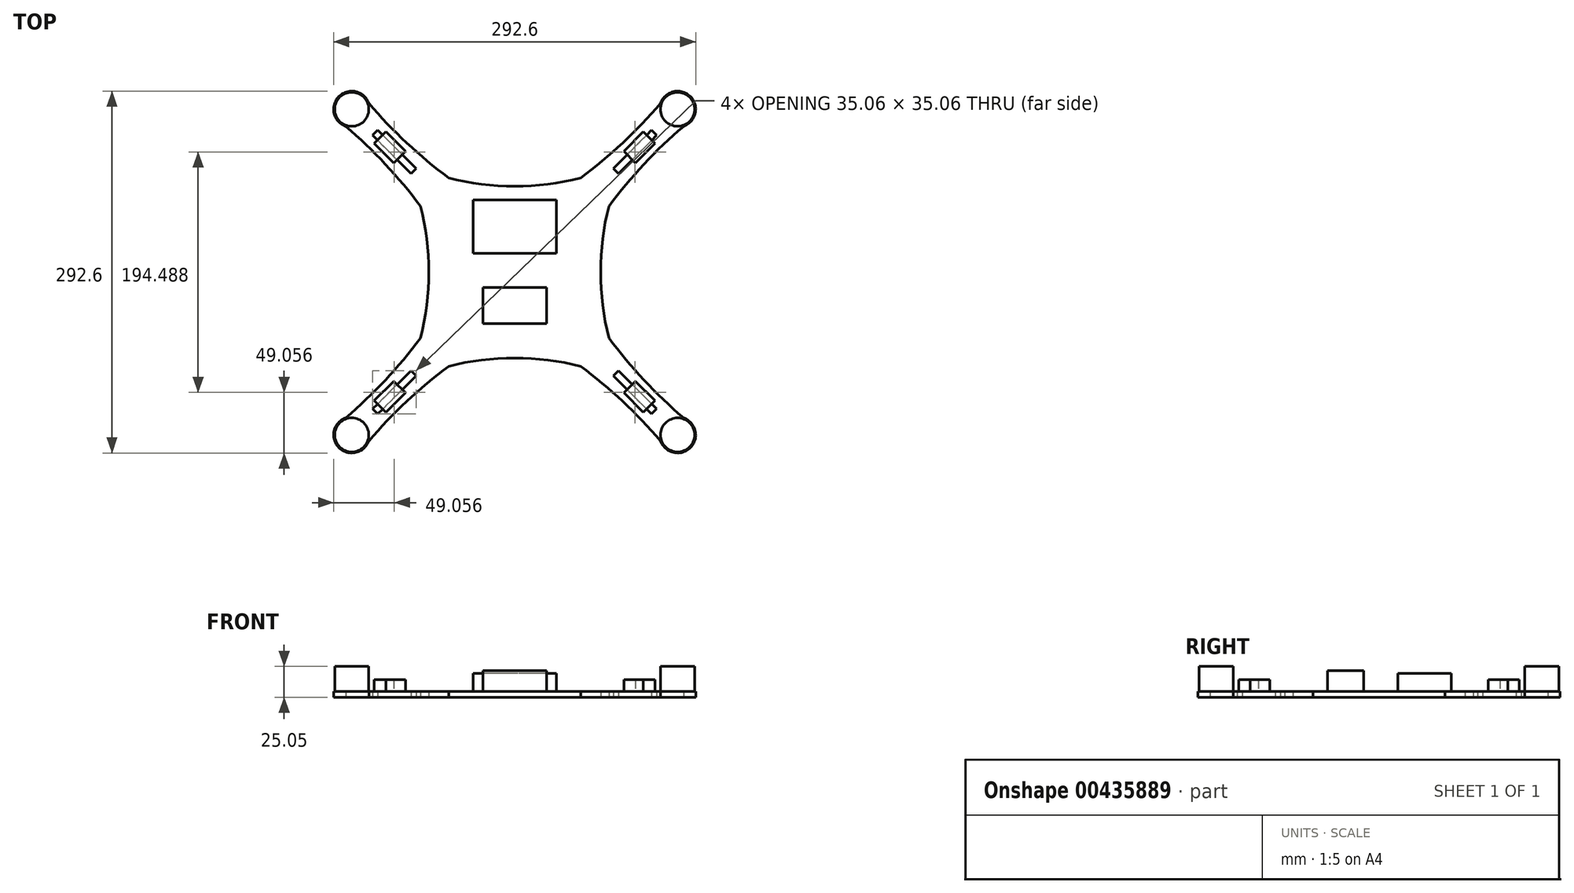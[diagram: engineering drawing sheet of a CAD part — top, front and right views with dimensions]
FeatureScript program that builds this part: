
annotation { "Feature Type Name" : "Feature", "Feature Type Description" : "" }
export const myFeature = defineFeature(function(context is Context, id is Id, definition is map)
    precondition{}
    {
        {
            var Q0;
            Q0=qCreatedBy(makeId("Top.planeOp"),FACE);
            var sketch = newSketch(context, id + "F0", { "sketchPlane" : qUnion([Q0])});
            skArc(sketch, "E0", {"start": v(-122.78, 142.2) * mm, "mid": v(-147.94, 147.94) * mm, "end": v(-142.2, 122.78) * mm});
            skArc(sketch, "E1.MirrorC", {"start": v(122.78, 142.2) * mm, "mid": v(147.94, 147.94) * mm, "end": v(142.2, 122.78) * mm});
            skArc(sketch, "E2.MirrorC", {"start": v(-122.78, -142.2) * mm, "mid": v(-147.94, -147.94) * mm, "end": v(-142.2, -122.78) * mm});
            skArc(sketch, "E3.MirrorC", {"start": v(122.78, -142.2) * mm, "mid": v(147.94, -147.94) * mm, "end": v(142.2, -122.78) * mm});
            skArc(sketch, "E4", {"start": v(79.33, 55.58) * mm, "mid": v(72.4, 0) * mm, "end": v(79.33, -55.58) * mm});
            skArc(sketch, "E5.MirrorCS", {"start": v(-79.33, 55.58) * mm, "mid": v(-72.4, 0) * mm, "end": v(-79.33, -55.58) * mm});
            skArc(sketch, "E6.1.0", {"start": v(-55.58, 79.33) * mm, "mid": v(0, 72.4) * mm, "end": v(55.58, 79.33) * mm});
            skArc(sketch, "E6.2.0", {"start": v(-79.33, -55.58) * mm, "mid": v(-72.4, 0) * mm, "end": v(-79.33, 55.58) * mm});
            skArc(sketch, "E6.3.0", {"start": v(55.58, -79.33) * mm, "mid": v(0, -72.4) * mm, "end": v(-55.58, -79.33) * mm});
            skArc(sketch, "E7", {"start": v(-142.2, -122.78) * mm, "mid": v(-108.9, -90.93) * mm, "end": v(-79.33, -55.58) * mm});
            skArc(sketch, "E8.MirrorCS", {"start": v(-122.78, -142.2) * mm, "mid": v(-90.93, -108.9) * mm, "end": v(-55.58, -79.33) * mm});
            skArc(sketch, "E9.MirrorCS", {"start": v(-142.2, 122.78) * mm, "mid": v(-108.9, 90.93) * mm, "end": v(-79.33, 55.58) * mm});
            skArc(sketch, "E10.MirrorCS", {"start": v(-122.78, 142.2) * mm, "mid": v(-90.93, 108.9) * mm, "end": v(-55.58, 79.33) * mm});
            skArc(sketch, "E11.MirrorCS", {"start": v(142.2, -122.78) * mm, "mid": v(108.9, -90.93) * mm, "end": v(79.33, -55.58) * mm});
            skArc(sketch, "E12.MirrorCS", {"start": v(122.78, -142.2) * mm, "mid": v(90.93, -108.9) * mm, "end": v(55.58, -79.33) * mm});
            skArc(sketch, "E13.MirrorCS", {"start": v(142.2, 122.78) * mm, "mid": v(108.9, 90.93) * mm, "end": v(79.33, 55.58) * mm});
            skArc(sketch, "E14.MirrorCS", {"start": v(122.78, 142.2) * mm, "mid": v(90.93, 108.9) * mm, "end": v(55.58, 79.33) * mm});
            skLineSegment(sketch, "E15", {"start": v(-117.4, 117.4) * mm, "end": v(-119.56, 115.25) * mm});
            skLineSegment(sketch, "E16", {"start": v(-87.34, 83.04) * mm, "end": v(-85.19, 85.19) * mm});
            skLineSegment(sketch, "E17.MirrorCS", {"start": v(-117.4, 117.4) * mm, "end": v(-115.25, 119.56) * mm});
            skLineSegment(sketch, "E18.MirrorCS", {"start": v(-83.04, 87.34) * mm, "end": v(-85.19, 85.19) * mm});
            skLineSegment(sketch, "E19", {"start": v(-119.56, 115.25) * mm, "end": v(-87.34, 83.04) * mm});
            skLineSegment(sketch, "E20", {"start": v(-115.25, 119.56) * mm, "end": v(-83.04, 87.34) * mm});
            skPoint(sketch, "E21.orphan", {"position": v(-113.1, 121.71) * mm});
            skPoint(sketch, "E22.orphan", {"position": v(-80.88, 89.5) * mm});
            skPoint(sketch, "E23.end.orphan", {"position": v(-89.5, 80.88) * mm});
            skPoint(sketch, "E24.orphan", {"position": v(-121.71, 113.1) * mm});
            skLineSegment(sketch, "E25", {"start": v(83.04, 87.34) * mm, "end": v(115.25, 119.56) * mm});
            skLineSegment(sketch, "E26", {"start": v(115.25, 119.56) * mm, "end": v(119.56, 115.25) * mm});
            skLineSegment(sketch, "E27", {"start": v(119.56, 115.25) * mm, "end": v(87.34, 83.04) * mm});
            skLineSegment(sketch, "E28", {"start": v(83.04, 87.34) * mm, "end": v(87.34, 83.04) * mm});
            skLineSegment(sketch, "E29", {"start": v(83.04, -87.34) * mm, "end": v(115.25, -119.56) * mm});
            skLineSegment(sketch, "E30", {"start": v(115.25, -119.56) * mm, "end": v(119.56, -115.25) * mm});
            skLineSegment(sketch, "E31", {"start": v(119.56, -115.25) * mm, "end": v(87.34, -83.04) * mm});
            skLineSegment(sketch, "E32", {"start": v(87.34, -83.04) * mm, "end": v(83.04, -87.34) * mm});
            skLineSegment(sketch, "E33", {"start": v(-119.56, -115.25) * mm, "end": v(-87.34, -83.04) * mm});
            skLineSegment(sketch, "E34", {"start": v(-87.34, -83.04) * mm, "end": v(-83.04, -87.34) * mm});
            skLineSegment(sketch, "E35", {"start": v(-83.04, -87.34) * mm, "end": v(-115.25, -119.56) * mm});
            skLineSegment(sketch, "E36", {"start": v(-115.25, -119.56) * mm, "end": v(-119.56, -115.25) * mm});
            skSolve(sketch);
        }
        {
            var Q0;
            Q0=makeQuery(id+"F0.imprint","IMPRINT",FACE,{"disambiguationData":[TD([[makeQuery(id+"F0.imprint","IMPRINT",EDGE,{"derivedFrom":sQuery(id+"F0.wireOp",EDGE,"E0")}),1.0]])]});
            extrude(context, id + "F1", {"entities" : qUnion([Q0]), "depth" : 4.76 * mm});
        }
        {
            var Q0;
            Q0=makeQuery(id+"F1.opExtrude","CAP_FACE",FACE,{"disambiguationData":[OSD([sQuery(id+"F0.wireOp",EDGE,"E0"),sQuery(id+"F0.wireOp",EDGE,"E1.MirrorC"),sQuery(id+"F0.wireOp",EDGE,"E2.MirrorC"),sQuery(id+"F0.wireOp",EDGE,"E3.MirrorC"),sQuery(id+"F0.wireOp",EDGE,"E4"),sQuery(id+"F0.wireOp",EDGE,"E6.1.0"),sQuery(id+"F0.wireOp",EDGE,"E6.2.0"),sQuery(id+"F0.wireOp",EDGE,"E6.3.0"),sQuery(id+"F0.wireOp",EDGE,"E7"),sQuery(id+"F0.wireOp",EDGE,"E8.MirrorCS"),sQuery(id+"F0.wireOp",EDGE,"E9.MirrorCS"),sQuery(id+"F0.wireOp",EDGE,"E10.MirrorCS"),sQuery(id+"F0.wireOp",EDGE,"E11.MirrorCS"),sQuery(id+"F0.wireOp",EDGE,"E12.MirrorCS"),sQuery(id+"F0.wireOp",EDGE,"E13.MirrorCS"),sQuery(id+"F0.wireOp",EDGE,"E14.MirrorCS"),sQuery(id+"F0.wireOp",EDGE,"E15"),sQuery(id+"F0.wireOp",EDGE,"E16"),sQuery(id+"F0.wireOp",EDGE,"E17.MirrorCS"),sQuery(id+"F0.wireOp",EDGE,"E18.MirrorCS"),sQuery(id+"F0.wireOp",EDGE,"E19"),sQuery(id+"F0.wireOp",EDGE,"E20"),sQuery(id+"F0.wireOp",EDGE,"E25"),sQuery(id+"F0.wireOp",EDGE,"E26"),sQuery(id+"F0.wireOp",EDGE,"E27"),sQuery(id+"F0.wireOp",EDGE,"E28"),sQuery(id+"F0.wireOp",EDGE,"E29"),sQuery(id+"F0.wireOp",EDGE,"E30"),sQuery(id+"F0.wireOp",EDGE,"E31"),sQuery(id+"F0.wireOp",EDGE,"E32"),sQuery(id+"F0.wireOp",EDGE,"E33"),sQuery(id+"F0.wireOp",EDGE,"E34"),sQuery(id+"F0.wireOp",EDGE,"E35"),sQuery(id+"F0.wireOp",EDGE,"E36")])],"isStart":false});
            var sketch = newSketch(context, id + "F2", { "sketchPlane" : qUnion([Q0])});
            skArc(sketch, "E37.0.0", {"start": v(55.58, -79.33) * mm, "mid": v(90.93, -108.9) * mm, "end": v(122.78, -142.2) * mm});
            skArc(sketch, "E37.0.1", {"start": v(122.78, -142.2) * mm, "mid": v(147.94, -147.94) * mm, "end": v(142.2, -122.78) * mm});
            skArc(sketch, "E37.0.2", {"start": v(142.2, -122.78) * mm, "mid": v(108.9, -90.93) * mm, "end": v(79.33, -55.58) * mm});
            skArc(sketch, "E37.0.3", {"start": v(79.33, -55.58) * mm, "mid": v(72.4, 0) * mm, "end": v(79.33, 55.58) * mm});
            skArc(sketch, "E37.0.4", {"start": v(79.33, 55.58) * mm, "mid": v(108.9, 90.93) * mm, "end": v(142.2, 122.78) * mm});
            skArc(sketch, "E37.0.5", {"start": v(142.2, 122.78) * mm, "mid": v(147.94, 147.94) * mm, "end": v(122.78, 142.2) * mm});
            skArc(sketch, "E37.0.6", {"start": v(122.78, 142.2) * mm, "mid": v(90.93, 108.9) * mm, "end": v(55.58, 79.33) * mm});
            skArc(sketch, "E37.0.7", {"start": v(55.58, 79.33) * mm, "mid": v(0, 72.4) * mm, "end": v(-55.58, 79.33) * mm});
            skArc(sketch, "E37.0.8", {"start": v(-55.58, 79.33) * mm, "mid": v(-90.93, 108.9) * mm, "end": v(-122.78, 142.2) * mm});
            skArc(sketch, "E37.0.9", {"start": v(-122.78, 142.2) * mm, "mid": v(-147.94, 147.94) * mm, "end": v(-142.2, 122.78) * mm});
            skArc(sketch, "E37.0.10", {"start": v(-142.2, 122.78) * mm, "mid": v(-108.9, 90.93) * mm, "end": v(-79.33, 55.58) * mm});
            skArc(sketch, "E37.0.11", {"start": v(-79.33, 55.58) * mm, "mid": v(-72.4, 0) * mm, "end": v(-79.33, -55.58) * mm});
            skArc(sketch, "E37.0.12", {"start": v(-79.33, -55.58) * mm, "mid": v(-108.9, -90.93) * mm, "end": v(-142.2, -122.78) * mm});
            skArc(sketch, "E37.0.13", {"start": v(-142.2, -122.78) * mm, "mid": v(-147.94, -147.94) * mm, "end": v(-122.78, -142.2) * mm});
            skArc(sketch, "E37.0.14", {"start": v(-122.78, -142.2) * mm, "mid": v(-90.93, -108.9) * mm, "end": v(-55.58, -79.33) * mm});
            skArc(sketch, "E37.0.15", {"start": v(-55.58, -79.33) * mm, "mid": v(0, -72.4) * mm, "end": v(55.58, -79.33) * mm});
            skCircle(sketch, "E38", {"center": v(-137.16, 137.16) * mm, "radius": 14.35 * mm});
            skCircle(sketch, "E39", {"center": v(137.16, 137.16) * mm, "radius": 14.35 * mm});
            skCircle(sketch, "E40", {"center": v(137.16, -137.16) * mm, "radius": 14.35 * mm});
            skCircle(sketch, "E41", {"center": v(-137.16, -137.16) * mm, "radius": 14.35 * mm});
            skLineSegment(sketch, "E42.bottom", {"start": v(35.05, 60.71) * mm, "end": v(-35.05, 60.71) * mm});
            skLineSegment(sketch, "E42.top", {"start": v(35.05, 15.76) * mm, "end": v(-35.05, 15.76) * mm});
            skLineSegment(sketch, "E42.left", {"start": v(35.05, 60.71) * mm, "end": v(35.05, 15.76) * mm});
            skLineSegment(sketch, "E42.right", {"start": v(-35.05, 60.71) * mm, "end": v(-35.05, 15.76) * mm});
            skPoint(sketch, "E42.middle", {"position": v(0, 38.23) * mm});
            skLineSegment(sketch, "E43.bottom", {"start": v(26.79, -13.03) * mm, "end": v(-26.79, -13.03) * mm});
            skLineSegment(sketch, "E43.top", {"start": v(26.79, -43.5) * mm, "end": v(-26.79, -43.5) * mm});
            skLineSegment(sketch, "E43.left", {"start": v(26.79, -13.03) * mm, "end": v(26.79, -43.5) * mm});
            skLineSegment(sketch, "E43.right", {"start": v(-26.79, -13.03) * mm, "end": v(-26.79, -43.5) * mm});
            skPoint(sketch, "E43.middle", {"position": v(0, -28.27) * mm});
            skLineSegment(sketch, "E44", {"start": v(-113.26, 113.26) * mm, "end": v(-118.18, 108.35) * mm});
            skLineSegment(sketch, "E45", {"start": v(-118.18, 108.35) * mm, "end": v(-101.7, 91.88) * mm});
            skLineSegment(sketch, "E46", {"start": v(-101.7, 91.88) * mm, "end": v(-96.79, 96.79) * mm});
            skLineSegment(sketch, "E47", {"start": v(0, 0) * mm, "end": v(0, 9.95) * mm});
            skLineSegment(sketch, "E48", {"start": v(0, 0) * mm, "end": v(8.33, 0) * mm});
            skLineSegment(sketch, "E49.MirrorCS", {"start": v(-113.26, 113.26) * mm, "end": v(-108.35, 118.18) * mm});
            skLineSegment(sketch, "E50.MirrorCS", {"start": v(-108.35, 118.18) * mm, "end": v(-91.88, 101.7) * mm});
            skLineSegment(sketch, "E51.MirrorCS", {"start": v(-91.88, 101.7) * mm, "end": v(-96.79, 96.79) * mm});
            skLineSegment(sketch, "E52.MirrorCS", {"start": v(113.26, 113.26) * mm, "end": v(118.18, 108.35) * mm});
            skLineSegment(sketch, "E53.MirrorCS", {"start": v(113.26, 113.26) * mm, "end": v(108.35, 118.18) * mm});
            skLineSegment(sketch, "E54.MirrorCS", {"start": v(108.35, 118.18) * mm, "end": v(91.88, 101.7) * mm});
            skLineSegment(sketch, "E55.MirrorCS", {"start": v(91.88, 101.7) * mm, "end": v(96.79, 96.79) * mm});
            skLineSegment(sketch, "E56.MirrorCS", {"start": v(101.7, 91.88) * mm, "end": v(96.79, 96.79) * mm});
            skLineSegment(sketch, "E57.MirrorCS", {"start": v(118.18, 108.35) * mm, "end": v(101.7, 91.88) * mm});
            skLineSegment(sketch, "E58.MirrorCS", {"start": v(108.35, -118.18) * mm, "end": v(91.88, -101.7) * mm});
            skLineSegment(sketch, "E59.MirrorCS", {"start": v(113.26, -113.26) * mm, "end": v(108.35, -118.18) * mm});
            skLineSegment(sketch, "E60.MirrorCS", {"start": v(113.26, -113.26) * mm, "end": v(118.18, -108.35) * mm});
            skLineSegment(sketch, "E61.MirrorCS", {"start": v(118.18, -108.35) * mm, "end": v(101.7, -91.88) * mm});
            skLineSegment(sketch, "E62.MirrorCS", {"start": v(101.7, -91.88) * mm, "end": v(96.79, -96.79) * mm});
            skLineSegment(sketch, "E63.MirrorCS", {"start": v(91.88, -101.7) * mm, "end": v(96.79, -96.79) * mm});
            skLineSegment(sketch, "E64.MirrorCS", {"start": v(-101.7, -91.88) * mm, "end": v(-96.79, -96.79) * mm});
            skLineSegment(sketch, "E65.MirrorCS", {"start": v(-91.88, -101.7) * mm, "end": v(-96.79, -96.79) * mm});
            skLineSegment(sketch, "E66.MirrorCS", {"start": v(-108.35, -118.18) * mm, "end": v(-91.88, -101.7) * mm});
            skLineSegment(sketch, "E67.MirrorCS", {"start": v(-113.26, -113.26) * mm, "end": v(-108.35, -118.18) * mm});
            skLineSegment(sketch, "E68.MirrorCS", {"start": v(-113.26, -113.26) * mm, "end": v(-118.18, -108.35) * mm});
            skLineSegment(sketch, "E69.MirrorCS", {"start": v(-118.18, -108.35) * mm, "end": v(-101.7, -91.88) * mm});
            skSolve(sketch);
        }
        {
            var Q0;
            Q0=makeQuery(id+"F2.imprint","IMPRINT",FACE,{"disambiguationData":[TD([[makeQuery(id+"F2.imprint","IMPRINT",EDGE,{"derivedFrom":sQuery(id+"F2.wireOp",EDGE,"E38")}),1.0]])]});
            var Q1;
            Q1=makeQuery(id+"F2.imprint","IMPRINT",FACE,{"disambiguationData":[TD([[makeQuery(id+"F2.imprint","IMPRINT",EDGE,{"derivedFrom":sQuery(id+"F2.wireOp",EDGE,"E39")}),1.0]])]});
            var Q2;
            Q2=makeQuery(id+"F2.imprint","IMPRINT",FACE,{"disambiguationData":[TD([[makeQuery(id+"F2.imprint","IMPRINT",EDGE,{"derivedFrom":sQuery(id+"F2.wireOp",EDGE,"E40")}),1.0]])]});
            var Q3;
            Q3=makeQuery(id+"F2.imprint","IMPRINT",FACE,{"disambiguationData":[TD([[makeQuery(id+"F2.imprint","IMPRINT",EDGE,{"derivedFrom":sQuery(id+"F2.wireOp",EDGE,"E41")}),1.0]])]});
            extrude(context, id + "F3", {"entities" : qUnion([Q0, Q1, Q2, Q3]), "operationType" : NewBodyOperationType.ADD, "depth" : 21.34 * mm});
        }
        {
            var Q0;
            {var subQ0=sQuery(id+"F2.wireOp",EDGE,"E50.MirrorCS");Q0=makeQuery(id+"F2.imprint","IMPRINT",FACE,{"disambiguationData":[TD([[makeQuery(id+"F2.imprint","IMPRINT",EDGE,{"derivedFrom":subQ0}),-1.0]])]});}
            var Q1;
            {var subQ5=sQuery(id+"F2.wireOp",EDGE,"E49.MirrorCS");var subQ9=sQuery(id+"F2.wireOp",EDGE,"E44");var subQ10=makeQuery(id+"F2.imprint","INTERSECT",VERTEX,{"derivedFrom":[subQ9,subQ5]});Q1=makeQuery(id+"F2.imprint","IMPRINT",FACE,{"disambiguationData":[TD([[makeQuery(id+"F2.imprint","IMPRINT",EDGE,{"disambiguationData":[TD([[subQ10,-1.0]])],"derivedFrom":subQ9}),1.0]])]});}
            var Q2;
            {var subQ0=sQuery(id+"F2.wireOp",EDGE,"E45");Q2=makeQuery(id+"F2.imprint","IMPRINT",FACE,{"disambiguationData":[TD([[makeQuery(id+"F2.imprint","IMPRINT",EDGE,{"derivedFrom":subQ0}),1.0]])]});}
            var Q3;
            {var subQ0=sQuery(id+"F2.wireOp",EDGE,"E57.MirrorCS");Q3=makeQuery(id+"F2.imprint","IMPRINT",FACE,{"disambiguationData":[TD([[makeQuery(id+"F2.imprint","IMPRINT",EDGE,{"derivedFrom":subQ0}),-1.0]])]});}
            var Q4;
            {var subQ7=sQuery(id+"F2.wireOp",EDGE,"E53.MirrorCS");var subQ8=sQuery(id+"F2.wireOp",EDGE,"E52.MirrorCS");var subQ9=makeQuery(id+"F2.imprint","INTERSECT",VERTEX,{"derivedFrom":[subQ8,subQ7]});Q4=makeQuery(id+"F2.imprint","IMPRINT",FACE,{"disambiguationData":[TD([[makeQuery(id+"F2.imprint","IMPRINT",EDGE,{"disambiguationData":[TD([[subQ9,-1.0]])],"derivedFrom":subQ8}),-1.0]])]});}
            var Q5;
            {var subQ0=sQuery(id+"F2.wireOp",EDGE,"E54.MirrorCS");Q5=makeQuery(id+"F2.imprint","IMPRINT",FACE,{"disambiguationData":[TD([[makeQuery(id+"F2.imprint","IMPRINT",EDGE,{"derivedFrom":subQ0}),1.0]])]});}
            var Q6;
            {var subQ0=sQuery(id+"F2.wireOp",EDGE,"E58.MirrorCS");Q6=makeQuery(id+"F2.imprint","IMPRINT",FACE,{"disambiguationData":[TD([[makeQuery(id+"F2.imprint","IMPRINT",EDGE,{"derivedFrom":subQ0}),-1.0]])]});}
            var Q7;
            {var subQ5=sQuery(id+"F2.wireOp",EDGE,"E59.MirrorCS");var subQ9=sQuery(id+"F2.wireOp",EDGE,"E60.MirrorCS");var subQ10=makeQuery(id+"F2.imprint","INTERSECT",VERTEX,{"derivedFrom":[subQ5,subQ9]});Q7=makeQuery(id+"F2.imprint","IMPRINT",FACE,{"disambiguationData":[TD([[makeQuery(id+"F2.imprint","IMPRINT",EDGE,{"disambiguationData":[TD([[subQ10,-1.0]])],"derivedFrom":subQ5}),-1.0]])]});}
            var Q8;
            {var subQ0=sQuery(id+"F2.wireOp",EDGE,"E61.MirrorCS");Q8=makeQuery(id+"F2.imprint","IMPRINT",FACE,{"disambiguationData":[TD([[makeQuery(id+"F2.imprint","IMPRINT",EDGE,{"derivedFrom":subQ0}),1.0]])]});}
            var Q9;
            {var subQ0=sQuery(id+"F2.wireOp",EDGE,"E69.MirrorCS");Q9=makeQuery(id+"F2.imprint","IMPRINT",FACE,{"disambiguationData":[TD([[makeQuery(id+"F2.imprint","IMPRINT",EDGE,{"derivedFrom":subQ0}),-1.0]])]});}
            var Q10;
            {var subQ7=sQuery(id+"F2.wireOp",EDGE,"E64.MirrorCS");var subQ9=sQuery(id+"F2.wireOp",EDGE,"E65.MirrorCS");var subQ10=makeQuery(id+"F2.imprint","INTERSECT",VERTEX,{"derivedFrom":[subQ7,subQ9]});Q10=makeQuery(id+"F2.imprint","IMPRINT",FACE,{"disambiguationData":[TD([[makeQuery(id+"F2.imprint","IMPRINT",EDGE,{"disambiguationData":[TD([[subQ10,1.0]])],"derivedFrom":subQ7}),-1.0]])]});}
            var Q11;
            {var subQ0=sQuery(id+"F2.wireOp",EDGE,"E66.MirrorCS");Q11=makeQuery(id+"F2.imprint","IMPRINT",FACE,{"disambiguationData":[TD([[makeQuery(id+"F2.imprint","IMPRINT",EDGE,{"derivedFrom":subQ0}),1.0]])]});}
            extrude(context, id + "F4", {"entities" : qUnion([Q0, Q1, Q2, Q3, Q4, Q5, Q6, Q7, Q8, Q9, Q10, Q11]), "operationType" : NewBodyOperationType.ADD, "depth" : 10.16 * mm});
        }
        {
            var Q0;
            Q0=makeQuery(id+"F2.imprint","IMPRINT",FACE,{"disambiguationData":[TD([[makeQuery(id+"F2.imprint","IMPRINT",EDGE,{"derivedFrom":sQuery(id+"F2.wireOp",EDGE,"E42.bottom")}),1.0]])]});
            extrude(context, id + "F5", {"entities" : qUnion([Q0]), "operationType" : NewBodyOperationType.ADD, "depth" : 15.24 * mm});
        }
        {
            var Q0;
            Q0=makeQuery(id+"F2.imprint","IMPRINT",FACE,{"disambiguationData":[TD([[makeQuery(id+"F2.imprint","IMPRINT",EDGE,{"derivedFrom":sQuery(id+"F2.wireOp",EDGE,"E43.bottom")}),1.0]])]});
            extrude(context, id + "F6", {"entities" : qUnion([Q0]), "operationType" : NewBodyOperationType.ADD, "depth" : 17.78 * mm});
        }
        {
            var Q0;
            Q0=makeQuery(id+"F1.opExtrude","SWEPT_BODY",BODY,{"disambiguationData":[OSD([sQuery(id+"F0.wireOp",EDGE,"E0"),sQuery(id+"F0.wireOp",EDGE,"E1.MirrorC"),sQuery(id+"F0.wireOp",EDGE,"E2.MirrorC"),sQuery(id+"F0.wireOp",EDGE,"E3.MirrorC"),sQuery(id+"F0.wireOp",EDGE,"E4"),sQuery(id+"F0.wireOp",EDGE,"E6.1.0"),sQuery(id+"F0.wireOp",EDGE,"E6.2.0"),sQuery(id+"F0.wireOp",EDGE,"E6.3.0"),sQuery(id+"F0.wireOp",EDGE,"E7"),sQuery(id+"F0.wireOp",EDGE,"E8.MirrorCS"),sQuery(id+"F0.wireOp",EDGE,"E9.MirrorCS"),sQuery(id+"F0.wireOp",EDGE,"E10.MirrorCS"),sQuery(id+"F0.wireOp",EDGE,"E11.MirrorCS"),sQuery(id+"F0.wireOp",EDGE,"E12.MirrorCS"),sQuery(id+"F0.wireOp",EDGE,"E13.MirrorCS"),sQuery(id+"F0.wireOp",EDGE,"E14.MirrorCS"),sQuery(id+"F0.wireOp",EDGE,"E15"),sQuery(id+"F0.wireOp",EDGE,"E16"),sQuery(id+"F0.wireOp",EDGE,"E17.MirrorCS"),sQuery(id+"F0.wireOp",EDGE,"E18.MirrorCS"),sQuery(id+"F0.wireOp",EDGE,"E19"),sQuery(id+"F0.wireOp",EDGE,"E20"),sQuery(id+"F0.wireOp",EDGE,"E25"),sQuery(id+"F0.wireOp",EDGE,"E26"),sQuery(id+"F0.wireOp",EDGE,"E27"),sQuery(id+"F0.wireOp",EDGE,"E28"),sQuery(id+"F0.wireOp",EDGE,"E29"),sQuery(id+"F0.wireOp",EDGE,"E30"),sQuery(id+"F0.wireOp",EDGE,"E31"),sQuery(id+"F0.wireOp",EDGE,"E32"),sQuery(id+"F0.wireOp",EDGE,"E33"),sQuery(id+"F0.wireOp",EDGE,"E34"),sQuery(id+"F0.wireOp",EDGE,"E35"),sQuery(id+"F0.wireOp",EDGE,"E36")])]});
            var Q1;
            Q1=qCreatedBy(makeId("Origin.pointOp"),VERTEX);
            transform(context, id + "F7", {"entities" : qUnion([Q0]), "transformType" : TransformType.SCALE_UNIFORMLY, "scale" : 0.96, "scalePoint" : qUnion([Q1]), "makeCopy" : false});
        }
    });
